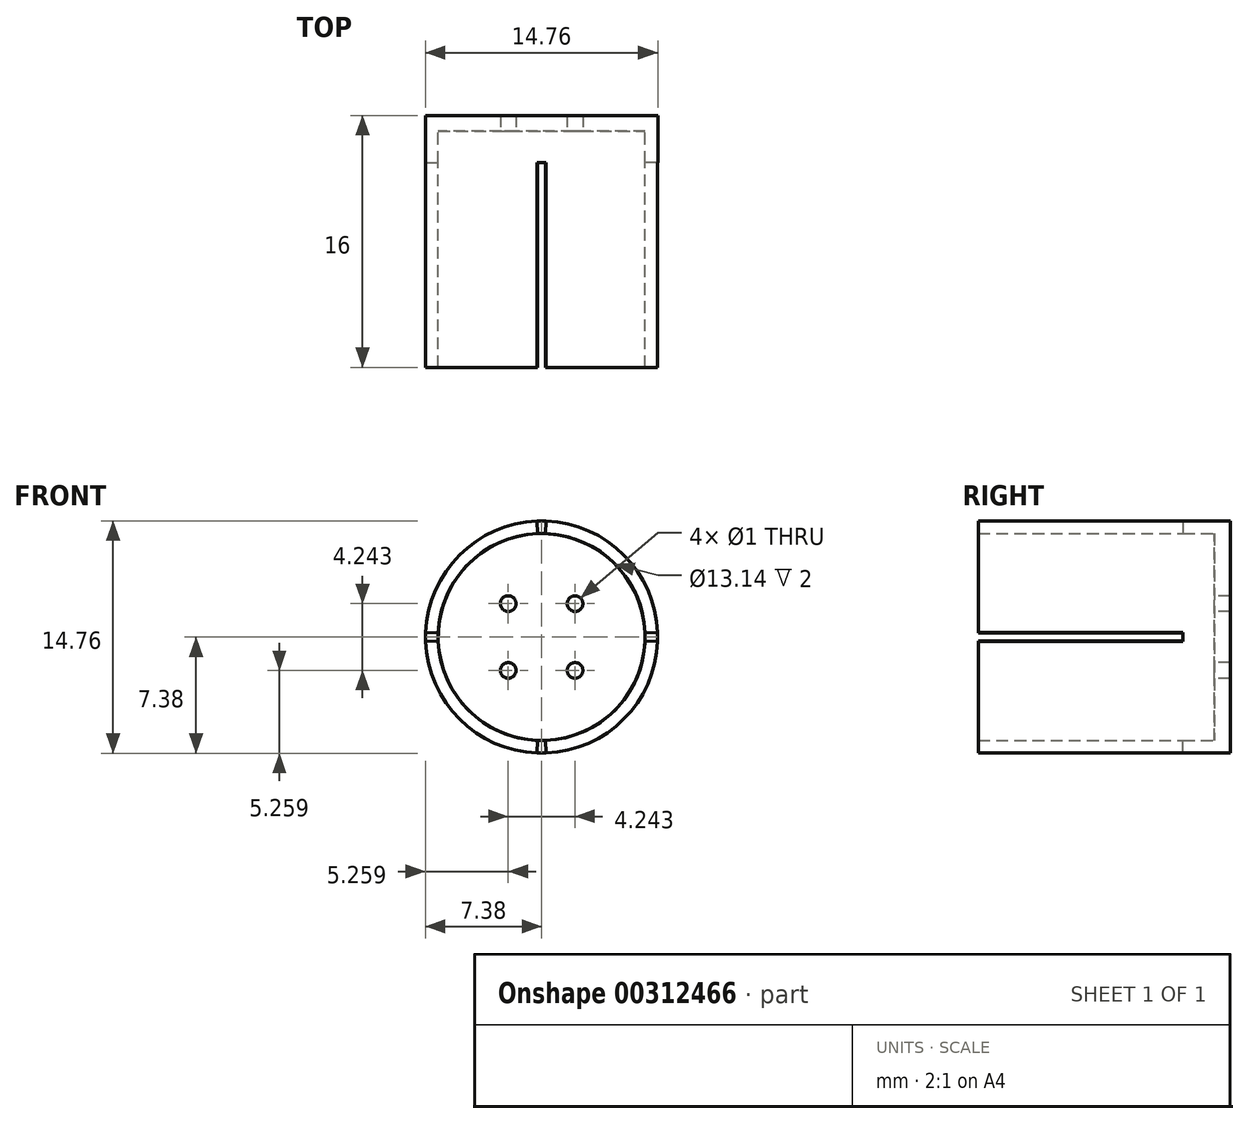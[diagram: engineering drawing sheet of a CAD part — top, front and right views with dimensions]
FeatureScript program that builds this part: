
annotation { "Feature Type Name" : "Feature", "Feature Type Description" : "" }
export const myFeature = defineFeature(function(context is Context, id is Id, definition is map)
    precondition{}
    {
        {
            var Q0;
            Q0=qCreatedBy(makeId("Front.planeOp"),FACE);
            var sketch = newSketch(context, id + "F0", { "sketchPlane" : qUnion([Q0])});
            skArc(sketch, "E0", {"start": v(6.57, 0.25) * mm, "mid": v(4.65, 4.65) * mm, "end": v(0.25, 6.57) * mm});
            skCircle(sketch, "E1.0", {"center": v(0, 0) * mm, "radius": 7.38 * mm});
            skLineSegment(sketch, "E2", {"start": v(0, 0) * mm, "end": v(-7.16, 7.16) * mm, "construction": true});
            skCircle(sketch, "E3", {"center": v(-2.12, 2.12) * mm, "radius": 0.5 * mm});
            skCircle(sketch, "E4.1.0", {"center": v(-2.12, -2.12) * mm, "radius": 0.5 * mm});
            skCircle(sketch, "E4.2.0", {"center": v(2.12, -2.12) * mm, "radius": 0.5 * mm});
            skCircle(sketch, "E4.3.0", {"center": v(2.12, 2.12) * mm, "radius": 0.5 * mm});
            skLineSegment(sketch, "E5", {"start": v(6.57, 0.25) * mm, "end": v(7.37, 0.28) * mm});
            skLineSegment(sketch, "E6.MirrorCS", {"start": v(6.57, -0.25) * mm, "end": v(7.37, -0.28) * mm});
            skLineSegment(sketch, "E7.1.0", {"start": v(-0.25, 6.57) * mm, "end": v(-0.28, 7.37) * mm});
            skLineSegment(sketch, "E7.1.1", {"start": v(0.25, 6.57) * mm, "end": v(0.28, 7.37) * mm});
            skLineSegment(sketch, "E7.2.0", {"start": v(-6.57, -0.25) * mm, "end": v(-7.37, -0.28) * mm});
            skLineSegment(sketch, "E7.2.1", {"start": v(-6.57, 0.25) * mm, "end": v(-7.37, 0.28) * mm});
            skLineSegment(sketch, "E7.3.0", {"start": v(0.25, -6.57) * mm, "end": v(0.28, -7.37) * mm});
            skLineSegment(sketch, "E7.3.1", {"start": v(-0.25, -6.57) * mm, "end": v(-0.28, -7.37) * mm});
            skArc(sketch, "E8.trimOffspring", {"start": v(0.25, -6.57) * mm, "mid": v(4.65, -4.65) * mm, "end": v(6.57, -0.25) * mm});
            skArc(sketch, "E9.trimOffspring", {"start": v(-6.57, -0.25) * mm, "mid": v(-4.65, -4.65) * mm, "end": v(-0.25, -6.57) * mm});
            skArc(sketch, "E10.trimOffspring", {"start": v(-0.25, 6.57) * mm, "mid": v(-4.65, 4.65) * mm, "end": v(-6.57, 0.25) * mm});
            skCircle(sketch, "E11", {"center": v(0, 0) * mm, "radius": 6.57 * mm});
            skSolve(sketch);
        }
        {
            var Q0;
            Q0=makeQuery(id+"F0.imprint","IMPRINT",FACE,{"disambiguationData":[TD([[makeQuery(id+"F0.imprint","IMPRINT",EDGE,{"derivedFrom":sQuery(id+"F0.wireOp",EDGE,"E0")}),-1.0]])]});
            var Q1;
            Q1=makeQuery(id+"F0.imprint","IMPRINT",FACE,{"disambiguationData":[TD([[makeQuery(id+"F0.imprint","IMPRINT",EDGE,{"derivedFrom":sQuery(id+"F0.wireOp",EDGE,"E0")}),1.0]])]});
            var Q2;
            {var subQ0=sQuery(id+"F0.wireOp",EDGE,"E7.1.0");Q2=makeQuery(id+"F0.imprint","IMPRINT",FACE,{"disambiguationData":[TD([[makeQuery(id+"F0.imprint","IMPRINT",EDGE,{"derivedFrom":subQ0}),1.0]])]});}
            var Q3;
            {var subQ0=sQuery(id+"F0.wireOp",EDGE,"E7.2.0");Q3=makeQuery(id+"F0.imprint","IMPRINT",FACE,{"disambiguationData":[TD([[makeQuery(id+"F0.imprint","IMPRINT",EDGE,{"derivedFrom":subQ0}),1.0]])]});}
            var Q4;
            {var subQ0=sQuery(id+"F0.wireOp",EDGE,"E6.MirrorCS");Q4=makeQuery(id+"F0.imprint","IMPRINT",FACE,{"disambiguationData":[TD([[makeQuery(id+"F0.imprint","IMPRINT",EDGE,{"derivedFrom":subQ0}),-1.0]])]});}
            var Q5;
            Q5=makeQuery(id+"F0.imprint","IMPRINT",FACE,{"disambiguationData":[TD([[makeQuery(id+"F0.imprint","IMPRINT",EDGE,{"derivedFrom":sQuery(id+"F0.wireOp",EDGE,"E3")}),-1.0]])]});
            extrude(context, id + "F1", {"entities" : qUnion([Q0, Q1, Q2, Q3, Q4, Q5]), "depth" : -1 * mm, "offsetDistance" : 25 * mm});
        }
        {
            var Q0;
            {var subQ0=sQuery(id+"F0.wireOp",EDGE,"E7.1.0");Q0=makeQuery(id+"F0.imprint","IMPRINT",FACE,{"disambiguationData":[TD([[makeQuery(id+"F0.imprint","IMPRINT",EDGE,{"derivedFrom":subQ0}),1.0]])]});}
            var Q1;
            Q1=makeQuery(id+"F0.imprint","IMPRINT",FACE,{"disambiguationData":[TD([[makeQuery(id+"F0.imprint","IMPRINT",EDGE,{"derivedFrom":sQuery(id+"F0.wireOp",EDGE,"E0")}),1.0]])]});
            var Q2;
            Q2=makeQuery(id+"F0.imprint","IMPRINT",FACE,{"disambiguationData":[TD([[makeQuery(id+"F0.imprint","IMPRINT",EDGE,{"derivedFrom":sQuery(id+"F0.wireOp",EDGE,"E0")}),-1.0]])]});
            var Q3;
            {var subQ0=sQuery(id+"F0.wireOp",EDGE,"E6.MirrorCS");Q3=makeQuery(id+"F0.imprint","IMPRINT",FACE,{"disambiguationData":[TD([[makeQuery(id+"F0.imprint","IMPRINT",EDGE,{"derivedFrom":subQ0}),-1.0]])]});}
            var Q4;
            {var subQ0=sQuery(id+"F0.wireOp",EDGE,"E7.2.0");Q4=makeQuery(id+"F0.imprint","IMPRINT",FACE,{"disambiguationData":[TD([[makeQuery(id+"F0.imprint","IMPRINT",EDGE,{"derivedFrom":subQ0}),1.0]])]});}
            extrude(context, id + "F2", {"entities" : qUnion([Q0, Q1, Q2, Q3, Q4]), "operationType" : NewBodyOperationType.ADD, "depth" : 2 * mm, "offsetDistance" : 25 * mm});
        }
        {
            var Q0;
            Q0=makeQuery(id+"F0.imprint","IMPRINT",FACE,{"disambiguationData":[TD([[makeQuery(id+"F0.imprint","IMPRINT",EDGE,{"derivedFrom":sQuery(id+"F0.wireOp",EDGE,"E0")}),-1.0]])]});
            var Q1;
            {var subQ0=sQuery(id+"F0.wireOp",EDGE,"E7.1.0");Q1=makeQuery(id+"F0.imprint","IMPRINT",FACE,{"disambiguationData":[TD([[makeQuery(id+"F0.imprint","IMPRINT",EDGE,{"derivedFrom":subQ0}),1.0]])]});}
            var Q2;
            {var subQ0=sQuery(id+"F0.wireOp",EDGE,"E7.2.0");Q2=makeQuery(id+"F0.imprint","IMPRINT",FACE,{"disambiguationData":[TD([[makeQuery(id+"F0.imprint","IMPRINT",EDGE,{"derivedFrom":subQ0}),1.0]])]});}
            var Q3;
            {var subQ0=sQuery(id+"F0.wireOp",EDGE,"E6.MirrorCS");Q3=makeQuery(id+"F0.imprint","IMPRINT",FACE,{"disambiguationData":[TD([[makeQuery(id+"F0.imprint","IMPRINT",EDGE,{"derivedFrom":subQ0}),-1.0]])]});}
            extrude(context, id + "F3", {"entities" : qUnion([Q0, Q1, Q2, Q3]), "operationType" : NewBodyOperationType.ADD, "depth" : 15 * mm, "offsetDistance" : 25 * mm});
        }
    });
